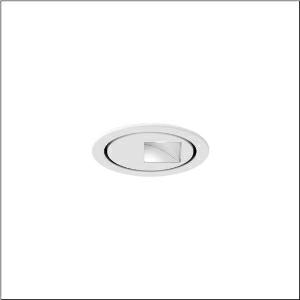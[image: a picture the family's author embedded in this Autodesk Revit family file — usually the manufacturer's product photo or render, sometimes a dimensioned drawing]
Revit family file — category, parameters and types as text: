
# Revit family: lunis_11_micro_round_51dj11b71wf21
name_source: partatom
category: Lighting Fixtures
units: mm (PartAtom-declared; Revit-internal decimal feet)

## family parameters
Cut with Voids When Loaded = No
Host = Face
Light Source = No
Part Type = Normal
Room Calculation Point = No
Round Connector Dimension = Use Diameter
Shared = No

## types (1)
- Lunis 11 micro round (1 x LED 3000K / CRI = 80 (unbekannt), 1320 lm, 3000K)
    Apparent Load = 20 VA
    CIE Flux Codes = 42 75 96 100 100
    Color Rendering = 80
    Color Temperature = 3000K
    Default Elevation = 1800 mm
    Description = Lunis 11 micro round, downlight, light control with wallwasher, of highly reflective aluminium, highly specular, light emission: direct distribution, LED rated luminous flux: 1.320lm, light colour: 830, with terminal, 3-pole, mains connection: 220..230V, AC, 50/60Hz, LED module, of aluminium, highly specular, white, diameter: 114mm, clamping range: 1..40mm, recessing ring, of plastic, traffic white (RAL 9016), protection rating (complete): IP20, insulation class (complete): insulation class II (safety insulation), certification: CE, permissible ambient temperature for indoor applications: 0..+35°C, packaging unit: 1 piece
    Height = 0 mm  [stored 0 ft]
    Lamp = 1 x LED 3000K / CRI >= 80 (unbekannt)
    Lamp Light Flux = 1320 lm
    Lamp count = 1
    Length = 114 mm
    Luminous efficacy = 67 lm/W
    Manufacturer = Siteco
    ModVariant = No
    Model = 51DJ11B71WF21
    Mounting Place = Ceiling
    Mounting Type = Recessed
    Number of Poles = 1
    OnlyDefault = Yes
    Power Factor = 1
    Product Name = Lunis 11 micro round
    Product group = downlight
    ProductGroupID = 400
    Protection Class = Protection class II
    Protection Degree = IP 20
    RLX_Detail_Level = 1
    RLX_Emergency_Light_Flux = 0 lm
    RLX_Emergency_Type = 0
    RLX_Emergency_Type_DB = No
    RlxData = <blob elided: 40893 chars, md5=df2ddd4d>
    Socket = socket
    Standby Power = 0 W
    System Light Flux = 1320 lm
    System Power = 20 W
    Type Comments = Product without accessories
    Type Image = l_1004773.jpg
    URL = http://relux.com
    VarID = ---
    Voltage = 0 V
    Weight = 0.00 kg
    Width = 114 mm

note: [stored X ft] marks values corroborated as IEEE doubles in the binary element streams (Revit-internal decimal feet)

## geometry (parser evidence)
native form markers: Blend x4, Sweep x10
no freeform markers — native parametric forms only
